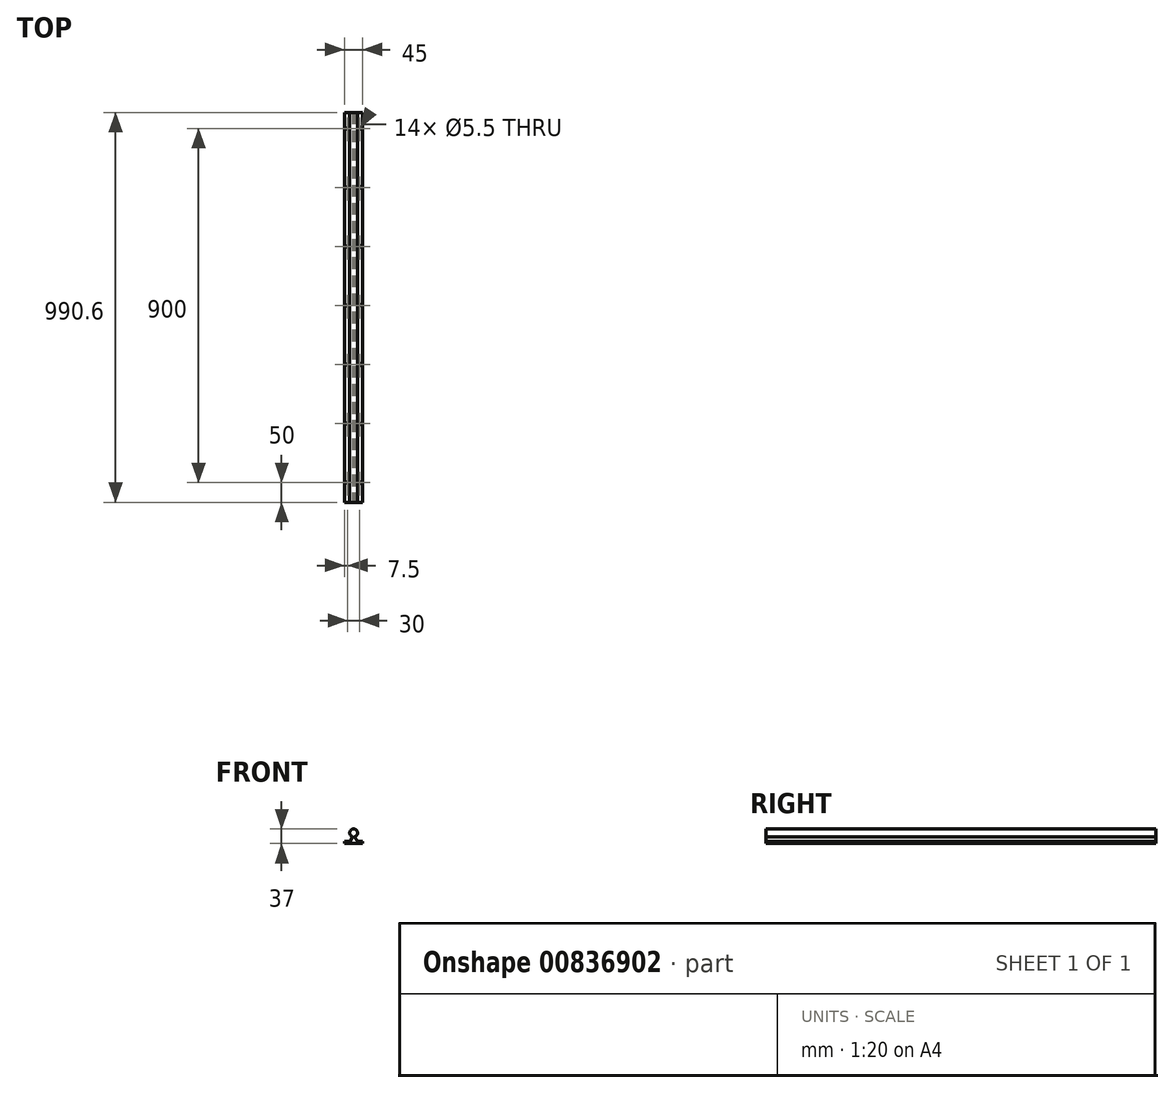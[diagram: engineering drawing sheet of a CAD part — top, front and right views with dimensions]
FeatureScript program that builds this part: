
annotation { "Feature Type Name" : "Feature", "Feature Type Description" : "" }
export const myFeature = defineFeature(function(context is Context, id is Id, definition is map)
    precondition{}
    {
        {
            var Q0;
            Q0=qCreatedBy(makeId("Front.planeOp"),FACE);
            var sketch = newSketch(context, id + "F0", { "sketchPlane" : qUnion([Q0])});
            skCircle(sketch, "E0", {"center": v(0, 0) * mm, "radius": 10 * mm});
            skLineSegment(sketch, "E1", {"start": v(-22.5, -27) * mm, "end": v(22.5, -27) * mm});
            skLineSegment(sketch, "E2", {"start": v(22.5, -27) * mm, "end": v(22.5, -22) * mm});
            skLineSegment(sketch, "E3", {"start": v(22.5, -22) * mm, "end": v(9.5, -22) * mm});
            skLineSegment(sketch, "E4", {"start": v(9.5, -22) * mm, "end": v(2.1, -9.17) * mm});
            skLineSegment(sketch, "E5", {"start": v(2.1, -9.17) * mm, "end": v(-2.1, -9.17) * mm});
            skLineSegment(sketch, "E6", {"start": v(-2.1, -9.17) * mm, "end": v(-9.5, -22) * mm});
            skLineSegment(sketch, "E7", {"start": v(-9.5, -22) * mm, "end": v(-22.5, -22) * mm});
            skLineSegment(sketch, "E8", {"start": v(-22.5, -22) * mm, "end": v(-22.5, -27) * mm});
            skLineSegment(sketch, "E9", {"start": v(0, -27) * mm, "end": v(0, 0) * mm, "construction": true});
            skLineSegment(sketch, "E10", {"start": v(0, -9.17) * mm, "end": v(0, -27) * mm, "construction": true});
            skSolve(sketch);
        }
        {
            var Q0;
            Q0 = qSketchRegion(id + "F0", true);
            extrude(context, id + "F1", {"entities" : qUnion([Q0]), "oppositeDirection" : true, "depth" : 990.6 * mm, "offsetDistance" : 25.4 * mm});
        }
        {
            var Q0;
            Q0=makeQuery(id+"F1.opExtrude","SWEPT_FACE",FACE,{"disambiguationData":[OSD([sQuery(id+"F0.wireOp",EDGE,"E3")])]});
            var sketch = newSketch(context, id + "F2", { "sketchPlane" : qUnion([Q0])});
            skCircle(sketch, "E11", {"center": v(15, 50) * mm, "radius": 2.75 * mm});
            skCircle(sketch, "E12", {"center": v(-15, 50) * mm, "radius": 2.75 * mm});
            skLineSegment(sketch, "E13", {"start": v(-15, 50) * mm, "end": v(15, 50) * mm, "construction": true});
            skLineSegment(sketch, "E14", {"start": v(0, 50) * mm, "end": v(0, 0) * mm, "construction": true});
            skCircle(sketch, "E15.0.1.0", {"center": v(15, 200) * mm, "radius": 2.75 * mm});
            skCircle(sketch, "E15.0.1.1", {"center": v(-15, 200) * mm, "radius": 2.75 * mm});
            skCircle(sketch, "E15.0.2.0", {"center": v(15, 350) * mm, "radius": 2.75 * mm});
            skCircle(sketch, "E15.0.2.1", {"center": v(-15, 350) * mm, "radius": 2.75 * mm});
            skCircle(sketch, "E15.0.3.0", {"center": v(15, 500) * mm, "radius": 2.75 * mm});
            skCircle(sketch, "E15.0.3.1", {"center": v(-15, 500) * mm, "radius": 2.75 * mm});
            skCircle(sketch, "E15.0.4.0", {"center": v(15, 650) * mm, "radius": 2.75 * mm});
            skCircle(sketch, "E15.0.4.1", {"center": v(-15, 650) * mm, "radius": 2.75 * mm});
            skCircle(sketch, "E15.0.5.0", {"center": v(15, 800) * mm, "radius": 2.75 * mm});
            skCircle(sketch, "E15.0.5.1", {"center": v(-15, 800) * mm, "radius": 2.75 * mm});
            skCircle(sketch, "E15.0.6.0", {"center": v(15, 950) * mm, "radius": 2.75 * mm});
            skCircle(sketch, "E15.0.6.1", {"center": v(-15, 950) * mm, "radius": 2.75 * mm});
            skCircle(sketch, "E15.1.0.0", {"center": v(88.15, 50) * mm, "radius": 2.75 * mm});
            skCircle(sketch, "E15.1.0.1", {"center": v(58.15, 50) * mm, "radius": 2.75 * mm});
            skCircle(sketch, "E15.1.1.0", {"center": v(88.15, 200) * mm, "radius": 2.75 * mm});
            skCircle(sketch, "E15.1.1.1", {"center": v(58.15, 200) * mm, "radius": 2.75 * mm});
            skCircle(sketch, "E15.1.2.0", {"center": v(88.15, 350) * mm, "radius": 2.75 * mm});
            skCircle(sketch, "E15.1.2.1", {"center": v(58.15, 350) * mm, "radius": 2.75 * mm});
            skCircle(sketch, "E15.1.3.0", {"center": v(88.15, 500) * mm, "radius": 2.75 * mm});
            skCircle(sketch, "E15.1.3.1", {"center": v(58.15, 500) * mm, "radius": 2.75 * mm});
            skCircle(sketch, "E15.1.4.0", {"center": v(88.15, 650) * mm, "radius": 2.75 * mm});
            skCircle(sketch, "E15.1.4.1", {"center": v(58.15, 650) * mm, "radius": 2.75 * mm});
            skCircle(sketch, "E15.1.5.0", {"center": v(88.15, 800) * mm, "radius": 2.75 * mm});
            skCircle(sketch, "E15.1.5.1", {"center": v(58.15, 800) * mm, "radius": 2.75 * mm});
            skCircle(sketch, "E15.1.6.0", {"center": v(88.15, 950) * mm, "radius": 2.75 * mm});
            skCircle(sketch, "E15.1.6.1", {"center": v(58.15, 950) * mm, "radius": 2.75 * mm});
            skCircle(sketch, "E15.2.0.0", {"center": v(161.3, 50) * mm, "radius": 2.75 * mm});
            skCircle(sketch, "E15.2.0.1", {"center": v(131.3, 50) * mm, "radius": 2.75 * mm});
            skCircle(sketch, "E15.2.1.0", {"center": v(161.3, 200) * mm, "radius": 2.75 * mm});
            skCircle(sketch, "E15.2.1.1", {"center": v(131.3, 200) * mm, "radius": 2.75 * mm});
            skCircle(sketch, "E15.2.2.0", {"center": v(161.3, 350) * mm, "radius": 2.75 * mm});
            skCircle(sketch, "E15.2.2.1", {"center": v(131.3, 350) * mm, "radius": 2.75 * mm});
            skCircle(sketch, "E15.2.3.0", {"center": v(161.3, 500) * mm, "radius": 2.75 * mm});
            skCircle(sketch, "E15.2.3.1", {"center": v(131.3, 500) * mm, "radius": 2.75 * mm});
            skCircle(sketch, "E15.2.4.0", {"center": v(161.3, 650) * mm, "radius": 2.75 * mm});
            skCircle(sketch, "E15.2.4.1", {"center": v(131.3, 650) * mm, "radius": 2.75 * mm});
            skCircle(sketch, "E15.2.5.0", {"center": v(161.3, 800) * mm, "radius": 2.75 * mm});
            skCircle(sketch, "E15.2.5.1", {"center": v(131.3, 800) * mm, "radius": 2.75 * mm});
            skCircle(sketch, "E15.2.6.0", {"center": v(161.3, 950) * mm, "radius": 2.75 * mm});
            skCircle(sketch, "E15.2.6.1", {"center": v(131.3, 950) * mm, "radius": 2.75 * mm});
            skLineSegment(sketch, "E15.direction1", {"start": v(15, 50) * mm, "end": v(88.15, 50) * mm, "construction": true});
            skLineSegment(sketch, "E15.direction2", {"start": v(15, 50) * mm, "end": v(15, 200) * mm, "construction": true});
            skSolve(sketch);
        }
        {
            var Q0;
            Q0 = qSketchRegion(id + "F2", true);
            extrude(context, id + "F3", {"entities" : qUnion([Q0]), "operationType" : NewBodyOperationType.REMOVE, "oppositeDirection" : true, "depth" : 25.4 * mm, "offsetDistance" : 25.4 * mm});
        }
    });
